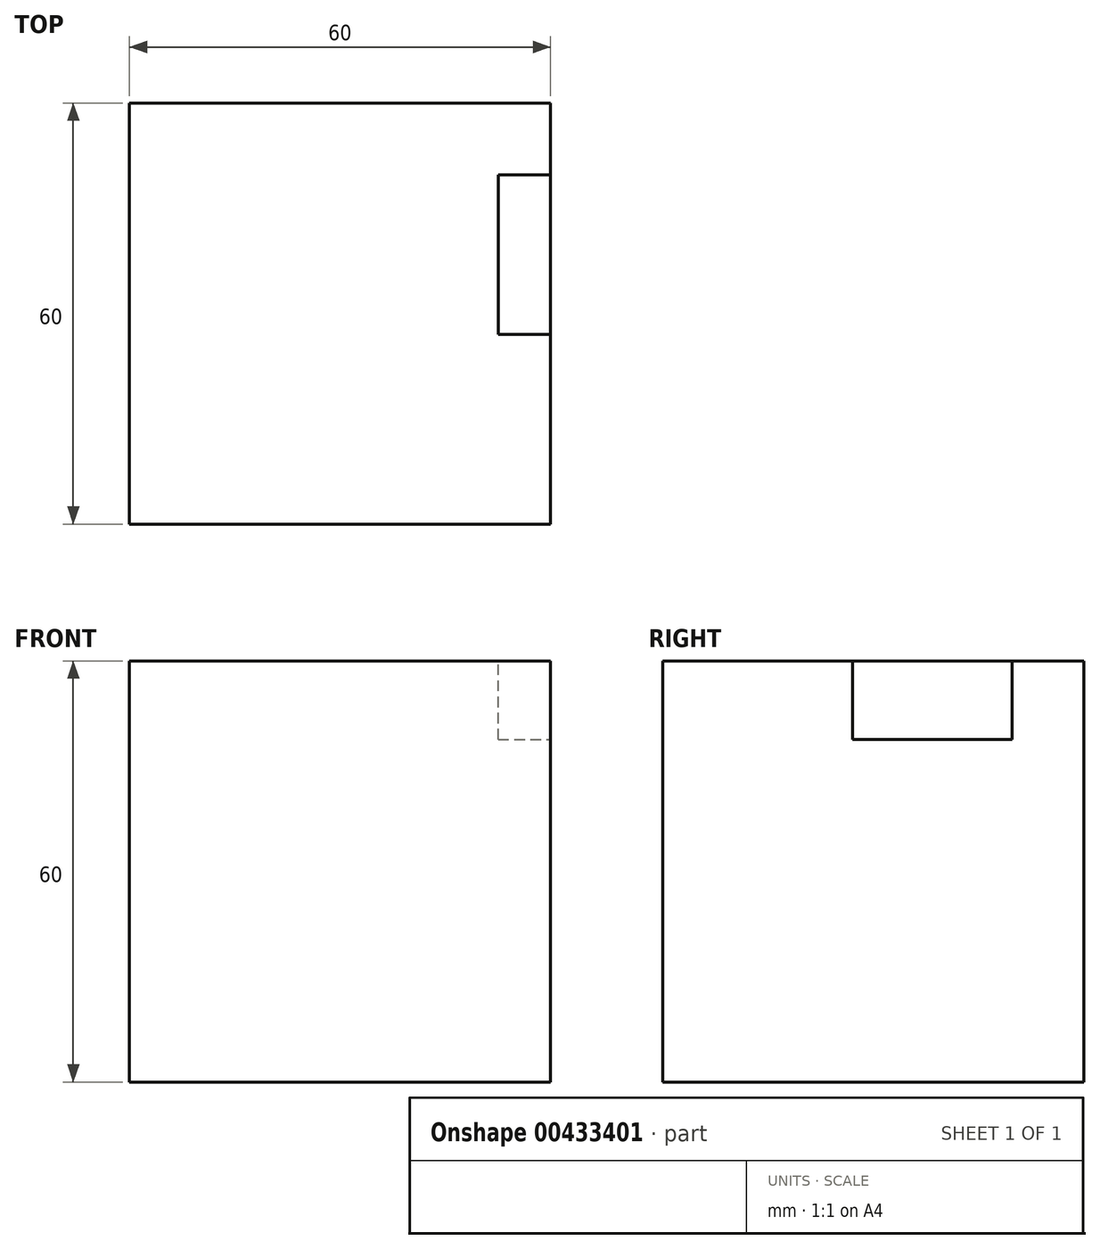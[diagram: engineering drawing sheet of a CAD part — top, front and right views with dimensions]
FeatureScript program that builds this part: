
annotation { "Feature Type Name" : "Feature", "Feature Type Description" : "" }
export const myFeature = defineFeature(function(context is Context, id is Id, definition is map)
    precondition{}
    {
        {
            var Q0;
            Q0=qCreatedBy(makeId("Top.planeOp"),FACE);
            var sketch = newSketch(context, id + "F0", { "sketchPlane" : qUnion([Q0])});
            skLineSegment(sketch, "E0.bottom", {"start": v(30, 30) * mm, "end": v(-30, 30) * mm});
            skLineSegment(sketch, "E0.top", {"start": v(30, -30) * mm, "end": v(-30, -30) * mm});
            skLineSegment(sketch, "E0.left", {"start": v(30, 30) * mm, "end": v(30, -30) * mm});
            skLineSegment(sketch, "E0.right", {"start": v(-30, 30) * mm, "end": v(-30, -30) * mm});
            skPoint(sketch, "E0.middle", {"position": v(0, 0) * mm});
            skSolve(sketch);
        }
        {
            var Q0;
            Q0=makeQuery(id+"F0.imprint","IMPRINT",FACE,{"disambiguationData":[TD([[makeQuery(id+"F0.imprint","IMPRINT",EDGE,{"derivedFrom":sQuery(id+"F0.wireOp",EDGE,"E0.bottom")}),1.0]])]});
            extrude(context, id + "F1", {"entities" : qUnion([Q0]), "depth" : 60 * mm});
        }
        {
            var Q0;
            Q0=makeQuery(id+"F1.opExtrude","CAP_FACE",FACE,{"disambiguationData":[OSD([sQuery(id+"F0.wireOp",EDGE,"E0.bottom"),sQuery(id+"F0.wireOp",EDGE,"E0.top"),sQuery(id+"F0.wireOp",EDGE,"E0.left"),sQuery(id+"F0.wireOp",EDGE,"E0.right")])],"isStart":false});
            var sketch = newSketch(context, id + "F2", { "sketchPlane" : qUnion([Q0])});
            skLineSegment(sketch, "E1.bottom", {"start": v(22.55, 19.75) * mm, "end": v(30, 19.75) * mm});
            skLineSegment(sketch, "E1.top", {"start": v(22.55, -2.96) * mm, "end": v(30, -2.96) * mm});
            skLineSegment(sketch, "E1.left", {"start": v(22.55, 19.75) * mm, "end": v(22.55, -2.96) * mm});
            skLineSegment(sketch, "E1.right", {"start": v(30, 19.75) * mm, "end": v(30, -2.96) * mm});
            skSolve(sketch);
        }
        {
            var Q0;
            Q0=makeQuery(id+"F2.imprint","IMPRINT",FACE,{"disambiguationData":[TD([[makeQuery(id+"F2.imprint","IMPRINT",EDGE,{"derivedFrom":sQuery(id+"F2.wireOp",EDGE,"E1.bottom")}),-1.0]])]});
            extrude(context, id + "F3", {"entities" : qUnion([Q0]), "operationType" : NewBodyOperationType.REMOVE, "oppositeDirection" : true, "depth" : 11.2 * mm, "offsetDistance" : 25 * mm});
        }
    });
